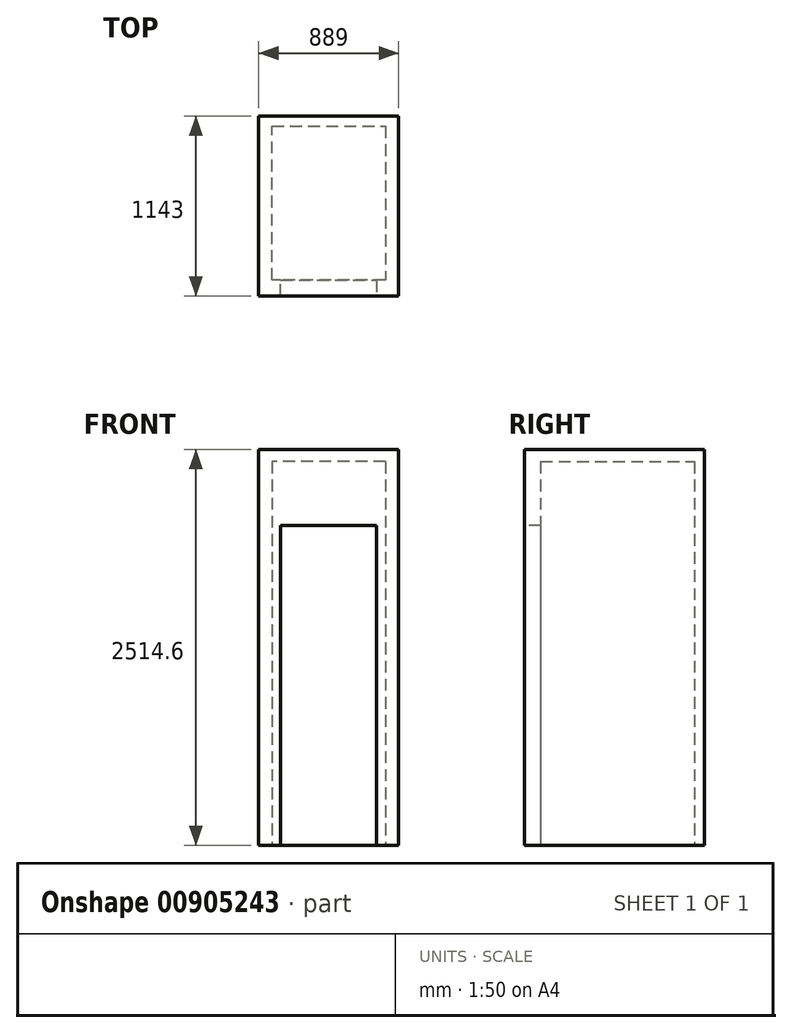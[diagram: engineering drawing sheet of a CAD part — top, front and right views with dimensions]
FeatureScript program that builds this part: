
annotation { "Feature Type Name" : "Feature", "Feature Type Description" : "" }
export const myFeature = defineFeature(function(context is Context, id is Id, definition is map)
    precondition{}
    {
        {
            var Q0;
            Q0=qCreatedBy(makeId("Top.planeOp"),FACE);
            var sketch = newSketch(context, id + "F0", { "sketchPlane" : qUnion([Q0])});
            skLineSegment(sketch, "E0.bottom", {"start": v(444.5, -571.5) * mm, "end": v(-444.5, -571.5) * mm});
            skLineSegment(sketch, "E0.top", {"start": v(444.5, 571.5) * mm, "end": v(-444.5, 571.5) * mm});
            skLineSegment(sketch, "E0.left", {"start": v(444.5, -571.5) * mm, "end": v(444.5, 571.5) * mm});
            skLineSegment(sketch, "E0.right", {"start": v(-444.5, -571.5) * mm, "end": v(-444.5, 571.5) * mm});
            skPoint(sketch, "E0.middle", {"position": v(0, 0) * mm});
            skSolve(sketch);
        }
        {
            var Q0;
            Q0=qSketchRegion(id+"F0",true);
            extrude(context, id + "F1", {"entities" : qUnion([Q0]), "depth" : 2514.6 * mm});
        }
        {
            var Q0;
            Q0=makeQuery(id+"F1.opExtrude","CAP_FACE",FACE,{"disambiguationData":[OSD([sQuery(id+"F0.wireOp",EDGE,"E0.bottom"),sQuery(id+"F0.wireOp",EDGE,"E0.top"),sQuery(id+"F0.wireOp",EDGE,"E0.left"),sQuery(id+"F0.wireOp",EDGE,"E0.right")])],"isStart":true});
            var sketch = newSketch(context, id + "F2", { "sketchPlane" : qUnion([Q0])});
            skLineSegment(sketch, "E1", {"start": v(-304.8, 571.5) * mm, "end": v(-304.8, 469.9) * mm});
            skLineSegment(sketch, "E2", {"start": v(-304.8, 469.9) * mm, "end": v(-360.36, 469.9) * mm});
            skLineSegment(sketch, "E3", {"start": v(-360.36, 469.9) * mm, "end": v(-360.36, -508) * mm});
            skLineSegment(sketch, "E4", {"start": v(-360.36, -508) * mm, "end": v(360.36, -508) * mm});
            skLineSegment(sketch, "E5", {"start": v(360.36, -508) * mm, "end": v(360.36, 469.9) * mm});
            skLineSegment(sketch, "E6", {"start": v(360.36, 469.9) * mm, "end": v(304.8, 469.9) * mm});
            skLineSegment(sketch, "E7", {"start": v(304.8, 469.9) * mm, "end": v(304.8, 571.5) * mm});
            skLineSegment(sketch, "E8", {"start": v(304.8, 571.5) * mm, "end": v(-304.8, 571.5) * mm});
            skLineSegment(sketch, "E9", {"start": v(0, -571.5) * mm, "end": v(0, -508) * mm});
            skSolve(sketch);
        }
        {
            var Q0;
            Q0=qSketchRegion(id+"F2",true);
            extrude(context, id + "F3", {"entities" : qUnion([Q0]), "operationType" : NewBodyOperationType.REMOVE, "oppositeDirection" : true, "depth" : 2438.4 * mm});
        }
        {
            var Q0;
            Q0=makeQuery(id+"F3.boolean.opBoolean","COPY",FACE,{"derivedFrom":makeQuery(id+"F3.opExtrude","CAP_FACE",FACE,{"disambiguationData":[OSD([sQuery(id+"F2.wireOp",EDGE,"E1"),sQuery(id+"F2.wireOp",EDGE,"E2"),sQuery(id+"F2.wireOp",EDGE,"E3"),sQuery(id+"F2.wireOp",EDGE,"E4"),sQuery(id+"F2.wireOp",EDGE,"E5"),sQuery(id+"F2.wireOp",EDGE,"E6"),sQuery(id+"F2.wireOp",EDGE,"E7"),sQuery(id+"F2.wireOp",EDGE,"E8")])],"isStart":false})});
            var sketch = newSketch(context, id + "F4", { "sketchPlane" : qUnion([Q0])});
            skLineSegment(sketch, "E10.bottom", {"start": v(-304.8, 571.5) * mm, "end": v(304.8, 571.5) * mm});
            skLineSegment(sketch, "E10.top", {"start": v(-304.8, 469.9) * mm, "end": v(304.8, 469.9) * mm});
            skLineSegment(sketch, "E10.left", {"start": v(-304.8, 571.5) * mm, "end": v(-304.8, 469.9) * mm});
            skLineSegment(sketch, "E10.right", {"start": v(304.8, 571.5) * mm, "end": v(304.8, 469.9) * mm});
            skSolve(sketch);
        }
        {
            var Q0;
            Q0=qSketchRegion(id+"F4",true);
            extrude(context, id + "F5", {"entities" : qUnion([Q0]), "operationType" : NewBodyOperationType.ADD, "depth" : 406.4 * mm});
        }
    });
